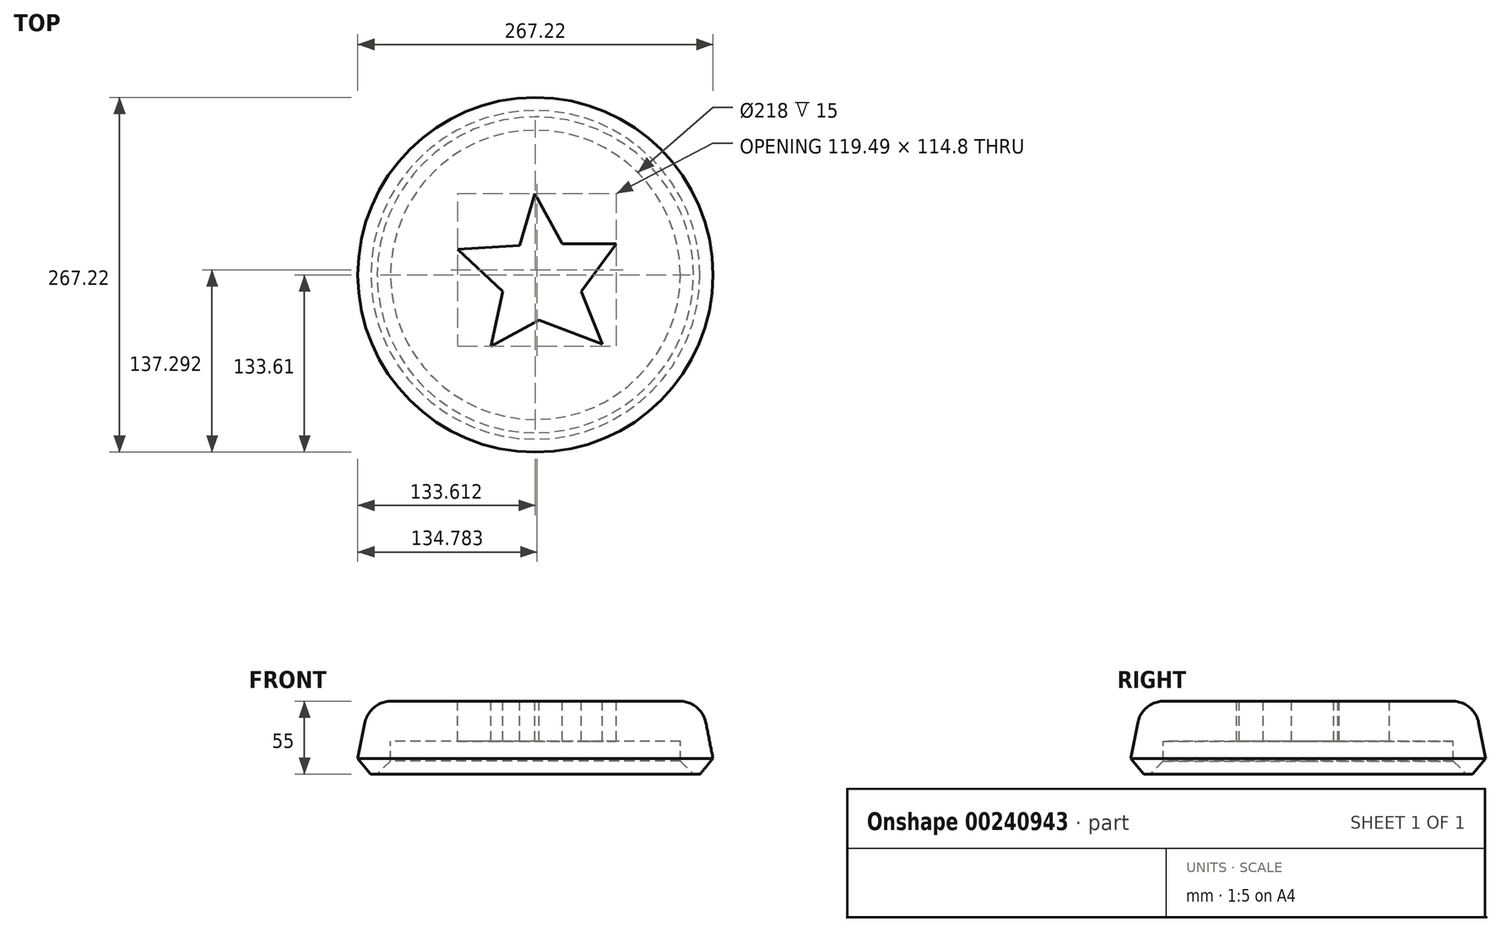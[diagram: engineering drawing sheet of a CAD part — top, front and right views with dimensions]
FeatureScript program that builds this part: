
annotation { "Feature Type Name" : "Feature", "Feature Type Description" : "" }
export const myFeature = defineFeature(function(context is Context, id is Id, definition is map)
    precondition{}
    {
        {
            var Q0;
            Q0=qCreatedBy(makeId("Front.planeOp"),FACE);
            var sketch = newSketch(context, id + "F0", { "sketchPlane" : qUnion([Q0])});
            skLineSegment(sketch, "E0", {"start": v(-72.34, 38.8) * mm, "end": v(52.66, 38.8) * mm});
            skLineSegment(sketch, "E1", {"start": v(52.66, 38.8) * mm, "end": v(52.66, 8.8) * mm});
            skLineSegment(sketch, "E2", {"start": v(52.66, 8.8) * mm, "end": v(-56.34, 8.8) * mm});
            skLineSegment(sketch, "E3", {"start": v(-56.34, 8.8) * mm, "end": v(-56.34, -16.2) * mm});
            skLineSegment(sketch, "E4", {"start": v(-56.34, -16.2) * mm, "end": v(-83.34, -16.2) * mm});
            skLineSegment(sketch, "E5", {"start": v(-83.34, -16.2) * mm, "end": v(-72.34, 38.8) * mm});
            skSolve(sketch);
        }
        {
            var Q0;
            Q0=makeQuery(id+"F0.imprint","IMPRINT",FACE,{"disambiguationData":[TD([[makeQuery(id+"F0.imprint","IMPRINT",EDGE,{"derivedFrom":sQuery(id+"F0.wireOp",EDGE,"E0")}),-1.0]])]});
            var Q1;
            Q1=sQuery(id+"F0.wireOp",EDGE,"E1");
            revolve(context, id + "F1", {"entities" : qUnion([Q0]), "axis" : qUnion([Q1]), "revolveType" : RevolveType.FULL});
        }
        {
            var Q0;
            Q0=makeQuery(id+"F1.opRevolve","SWEPT_EDGE",EDGE,{"disambiguationData":[OSD([sQuery(id+"F0.wireOp",EDGE,"E0"),sQuery(id+"F0.wireOp",EDGE,"E5")])]});
            fillet(context, id + "F2", {"entities" : qUnion([Q0]), "radius" : 20 * mm, "tangentPropagation" : true, "allowEdgeOverflow" : false});
        }
        {
            var Q0;
            Q0=makeQuery(id+"F1.opRevolve","SWEPT_EDGE",EDGE,{"disambiguationData":[OSD([sQuery(id+"F0.wireOp",EDGE,"E4"),sQuery(id+"F0.wireOp",EDGE,"E5")])]});
            var Q1;
            Q1=makeQuery(id+"F1.opRevolve","SWEPT_EDGE",EDGE,{"disambiguationData":[OSD([sQuery(id+"F0.wireOp",EDGE,"E3"),sQuery(id+"F0.wireOp",EDGE,"E4")])]});
            chamfer(context, id + "F3", {"entities" : qUnion([Q0, Q1]), "width" : 10 * mm, "tangentPropagation" : true});
        }
        {
            var Q0;
            Q0=makeQuery(id+"F1.opRevolve","SWEPT_FACE",FACE,{"disambiguationData":[OSD([sQuery(id+"F0.wireOp",EDGE,"E0")])]});
            var sketch = newSketch(context, id + "F4", { "sketchPlane" : qUnion([Q0])});
            skLineSegment(sketch, "E6", {"start": v(52.33, 61.08) * mm, "end": v(72.74, 23.26) * mm});
            skLineSegment(sketch, "E7", {"start": v(72.74, 23.26) * mm, "end": v(113.58, 23.26) * mm});
            skLineSegment(sketch, "E8", {"start": v(113.58, 23.26) * mm, "end": v(87.14, -12.55) * mm});
            skLineSegment(sketch, "E9", {"start": v(87.14, -12.55) * mm, "end": v(103.2, -52.05) * mm});
            skLineSegment(sketch, "E10", {"start": v(103.2, -52.05) * mm, "end": v(55.34, -33.97) * mm});
            skLineSegment(sketch, "E11", {"start": v(55.34, -33.97) * mm, "end": v(19.2, -53.72) * mm});
            skLineSegment(sketch, "E12", {"start": v(19.2, -53.72) * mm, "end": v(28.23, -12.55) * mm});
            skLineSegment(sketch, "E13", {"start": v(28.23, -12.55) * mm, "end": v(-5.91, 19.25) * mm});
            skLineSegment(sketch, "E14", {"start": v(-5.91, 19.25) * mm, "end": v(40.95, 22.26) * mm});
            skLineSegment(sketch, "E15", {"start": v(40.95, 22.26) * mm, "end": v(52.33, 61.08) * mm});
            skSolve(sketch);
        }
        {
            var Q0;
            Q0=makeQuery(id+"F4.imprint","IMPRINT",FACE,{"disambiguationData":[TD([[makeQuery(id+"F4.imprint","IMPRINT",EDGE,{"derivedFrom":sQuery(id+"F4.wireOp",EDGE,"E6")}),-1.0]])]});
            extrude(context, id + "F5", {"entities" : qUnion([Q0]), "operationType" : NewBodyOperationType.REMOVE, "oppositeDirection" : true, "depth" : 224 * mm});
        }
    });
